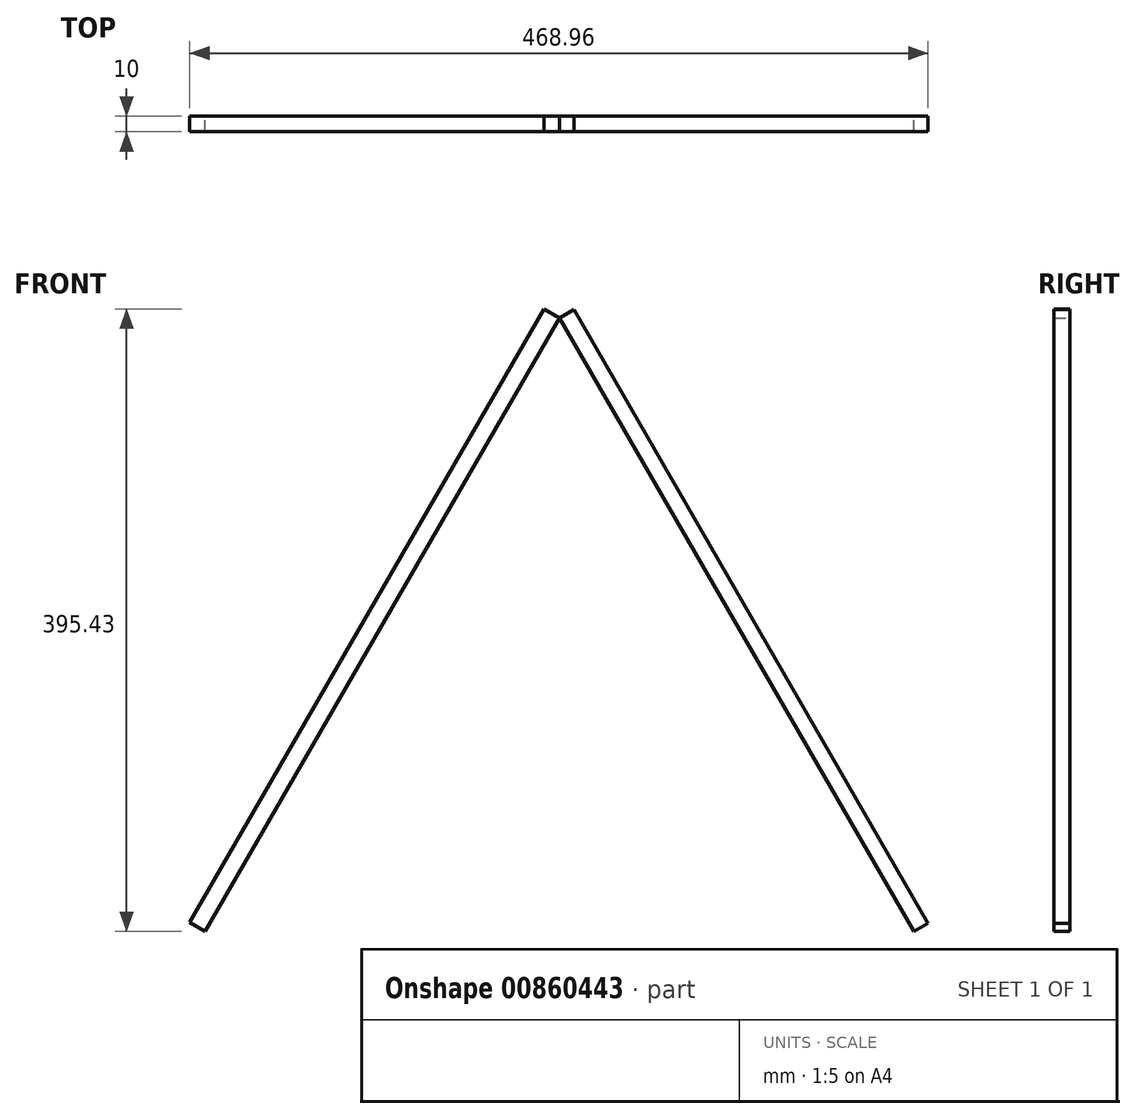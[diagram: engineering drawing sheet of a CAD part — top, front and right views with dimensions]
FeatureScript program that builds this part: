
annotation { "Feature Type Name" : "Feature", "Feature Type Description" : "" }
export const myFeature = defineFeature(function(context is Context, id is Id, definition is map)
    precondition{}
    {
        {
            var Q0;
            Q0=qCreatedBy(makeId("Front.planeOp"),FACE);
            var sketch = newSketch(context, id + "F0", { "sketchPlane" : qUnion([Q0])});
            skCircle(sketch, "E0.cCircle", {"center": v(0, 0) * mm, "radius": 129.9 * mm, "construction": true});
            skLineSegment(sketch, "E0.0", {"start": v(225, -129.9) * mm, "end": v(-225, -129.9) * mm});
            skLineSegment(sketch, "E0.1", {"start": v(-225, -129.9) * mm, "end": v(0, 259.8) * mm});
            skLineSegment(sketch, "E0.2", {"start": v(0, 259.8) * mm, "end": v(225, -129.9) * mm});
            skPoint(sketch, "E0.0.midPoint", {"position": v(0, -129.9) * mm});
            skLineSegment(sketch, "E1", {"start": v(0, 259.8) * mm, "end": v(9.04, 265.03) * mm});
            skLineSegment(sketch, "E2", {"start": v(9.04, 265.03) * mm, "end": v(234.04, -124.68) * mm});
            skLineSegment(sketch, "E3", {"start": v(225, -129.9) * mm, "end": v(234.04, -124.68) * mm});
            skLineSegment(sketch, "E4", {"start": v(0, 259.8) * mm, "end": v(-9.92, 265.53) * mm});
            skLineSegment(sketch, "E5", {"start": v(-9.92, 265.53) * mm, "end": v(-234.92, -124.18) * mm});
            skLineSegment(sketch, "E6", {"start": v(-234.92, -124.18) * mm, "end": v(-225, -129.9) * mm});
            skSolve(sketch);
        }
        {
            var Q0;
            Q0=makeQuery(id+"F0.imprint","IMPRINT",FACE,{"disambiguationData":[TD([[makeQuery(id+"F0.imprint","IMPRINT",EDGE,{"derivedFrom":sQuery(id+"F0.wireOp",EDGE,"E0.1")}),1.0]])]});
            var Q1;
            Q1=makeQuery(id+"F0.imprint","IMPRINT",FACE,{"disambiguationData":[TD([[makeQuery(id+"F0.imprint","IMPRINT",EDGE,{"derivedFrom":sQuery(id+"F0.wireOp",EDGE,"E0.2")}),1.0]])]});
            extrude(context, id + "F1", {"entities" : qUnion([Q0, Q1]), "depth" : 10 * mm, "offsetDistance" : 25 * mm});
        }
    });
